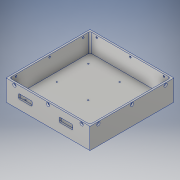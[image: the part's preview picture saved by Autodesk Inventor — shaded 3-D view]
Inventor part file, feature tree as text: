
AUTODESK INVENTOR PART (.ipt)
format: ipt  version: 2018 (Build 220112000, 112)  size: 263,680 bytes
history: native  units: in
note: dims shown in document units (in); Inventor stores cm internally (conversion verified against a paired STEP export)
features: thread x21, sketch x8, hole x5, extrude x3, fillet x2
ambient origin geometry x8: Origin, YZ Plane, XZ Plane, XY Plane, X Axis, Y Axis, Z Axis, Center Point
bodies: Solid1 (feature_tree)
feature tree (39):
  extrude  "Extrusion1"  Depth=7.874in
  extrude  "Extrusion2"  Depth=7.5591in
  sketch  "Sketch3"  dims[d6=0.1575in d7=0.1575in]
  sketch  "Sketch4"  dims[d8=1.7323in d9=0.0in d10=6.6929in]
  sketch  "Sketch5"  dims[d11=6.6929in d12=0.4331in]
  fillet  "Fillet1"  Radius=7.5591in
  extrude  "Extrusion8"  Depth=0.1575in
  hole  "Hole1"  [1 undecoded]
  hole  "Hole2"  [1 undecoded]
  hole  "Hole3"  [1 undecoded]
  hole  "Hole4"  [1 undecoded]
  hole  "Hole5"  [1 undecoded]
  thread  "Thread25"  [1 undecoded]
  thread  "Thread26"  [1 undecoded]
  thread  "Thread27"  [1 undecoded]
  thread  "Thread28"  [1 undecoded]
  thread  "Thread29"  [1 undecoded]
  thread  "Thread30"  [1 undecoded]
  thread  "Thread31"  [1 undecoded]
  thread  "Thread32"  [1 undecoded]
  thread  "Thread33"  [1 undecoded]
  thread  "Thread34"  [1 undecoded]
  thread  "Thread35"  [1 undecoded]
  thread  "Thread36"  [1 undecoded]
  thread  "Thread37"  [1 undecoded]
  thread  "Thread38"  [1 undecoded]
  thread  "Thread39"  [1 undecoded]
  thread  "Thread40"  [1 undecoded]
  thread  "Thread41"  [1 undecoded]
  thread  "Thread42"  [1 undecoded]
  thread  "Thread43"  [1 undecoded]
  thread  "Thread44"  [1 undecoded]
  thread  "Thread45"  [1 undecoded]
  fillet  "Fillet2"  Radius=0.3937in
  sketch  "Sketch1"  dims[d0=7.874in d1=7.874in]
  sketch  "Sketch2"  dims[d2=1.9685in d3=0.0in d4=7.5591in d5=7.5591in]
  sketch  "Sketch8"  dims[d15=0.3937in d16=0.3937in]
  sketch  "Sketch9"  dims[d17=1.1811in d19=2.9528in d20=1.1811in d22=2.9528in d25=0.1575in d27=0.1969in d29=0.7874in d30=1.1811in d32=3.1496in d33=0.3937in d35=0.3937in d43=0.1575in d44=0.1969in d45=0.7874in d46=1.1811in d48=3.1496in d49=0.3937in d51=0.3937in d103=0.1575in d114=1.2598in d115=0.4331in d116=1.2598in d117=0.4331in d121=2.5591in d122=1.1811in d123=0.8661in d124=0.8661in d125=0.3937in d126=0.0in d127=0.1181in d128=0.2362in d129=0.1575in d130=0.0787in d131=90.0deg d132=0.1969in d133=0.8108in d134=0.1575in d135=0.2362in d136=0.315in d137=0.0787in d138=90.0deg d139=0.315in d140=0.8108in d141=0.1575in d142=0.2362in d143=0.315in d144=0.0787in d145=90.0deg d146=0.315in d147=0.8108in d148=0.3937in d149=0.0in d150=0.3937in d151=0.0in d152=0.3937in d153=0.0in d154=0.3937in d155=0.0in d156=0.3937in d157=0.0in d158=0.3937in d159=0.0in d160=0.3937in d161=0.0in d162=0.3937in d163=0.0in d164=0.3937in d165=0.0in d166=0.3937in d167=0.0in d169=1.1811in d171=0.3937in d172=0.1575in d173=0.1969in d174=0.7874in d175=3.1496in d176=0.3937in d177=0.1575in d178=0.2362in d179=0.315in d180=0.0787in d181=90.0deg d182=0.315in d183=0.8108in d185=1.1811in d187=0.3937in d188=0.1575in d189=0.1969in d190=0.7874in d191=3.1496in d192=0.3937in d194=1.1811in d196=0.3937in d197=0.1575in d198=0.1969in d199=0.7874in d200=3.1496in d201=0.3937in d203=1.1811in d205=0.3937in d206=0.1575in d207=0.1969in d208=0.7874in d209=3.1496in d210=0.3937in d211=0.1575in d212=0.2362in d213=0.315in d214=0.0787in d215=90.0deg d216=0.315in d217=0.8108in d218=0.3937in d219=0.0in d220=0.3937in d221=0.0in d222=0.3937in d223=0.0in d224=0.3937in d225=0.0in d226=0.3937in d227=0.0in d228=0.3937in d229=0.0in d230=0.3937in d231=0.0in d232=0.3937in d233=0.0in d234=0.3937in d235=0.0in d236=0.3937in d237=0.0in d238=0.3937in d239=0.0in d240=0.0787in]
  sketch  "Sketch7"  dims[d13=0.2756in d14=0.1181in]
note: 26 required parameter values undecoded (feature->parameter linkage not recoverable at this tier; creation-order binding heuristic only, values carry confidence <= 0.55)
